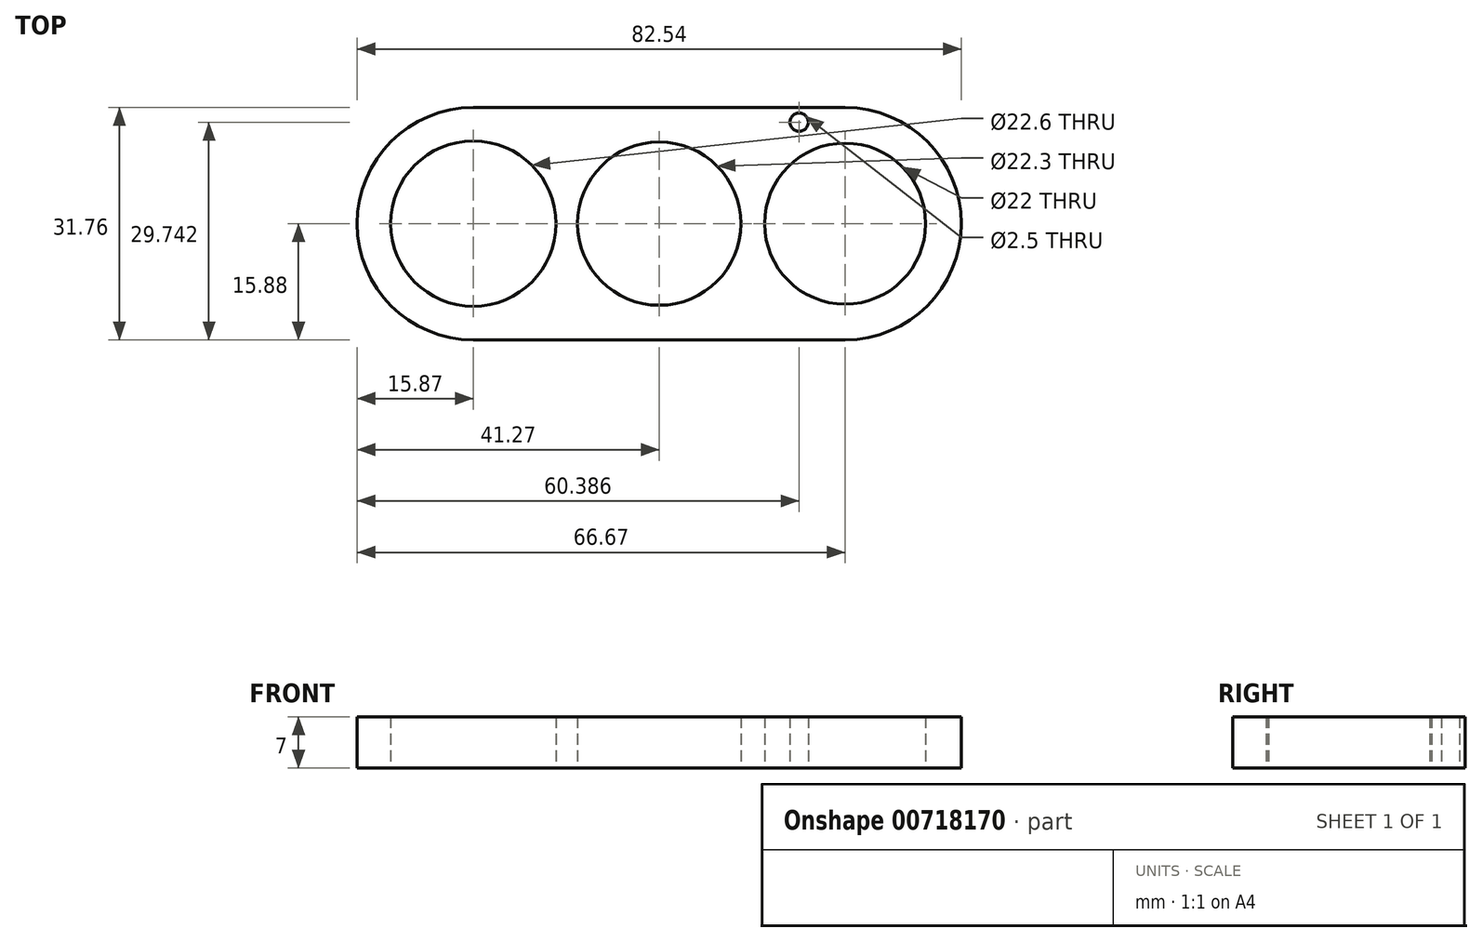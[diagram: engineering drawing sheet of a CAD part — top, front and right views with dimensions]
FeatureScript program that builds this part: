
annotation { "Feature Type Name" : "Feature", "Feature Type Description" : "" }
export const myFeature = defineFeature(function(context is Context, id is Id, definition is map)
    precondition{}
    {
        {
            var Q0;
            Q0=qCreatedBy(makeId("Top.planeOp"),FACE);
            var sketch = newSketch(context, id + "F0", { "sketchPlane" : qUnion([Q0])});
            skCircle(sketch, "E0", {"center": v(-25.4, 0) * mm, "radius": 11.3 * mm});
            skCircle(sketch, "E1", {"center": v(0, 0) * mm, "radius": 11.15 * mm});
            skCircle(sketch, "E2", {"center": v(25.4, 0) * mm, "radius": 11 * mm});
            skLineSegment(sketch, "E3", {"start": v(-25.4, 0) * mm, "end": v(0, 0) * mm, "construction": true});
            skLineSegment(sketch, "E4", {"start": v(25.4, 0) * mm, "end": v(0, 0) * mm, "construction": true});
            skLineSegment(sketch, "E5.bottom", {"start": v(-25.4, 15.88) * mm, "end": v(25.4, 15.88) * mm});
            skLineSegment(sketch, "E5.top", {"start": v(-25.4, -15.88) * mm, "end": v(25.4, -15.88) * mm});
            skLineSegment(sketch, "E5.left", {"start": v(-25.4, 15.88) * mm, "end": v(-25.4, -15.88) * mm, "construction": true});
            skLineSegment(sketch, "E5.right", {"start": v(25.4, 15.88) * mm, "end": v(25.4, -15.88) * mm, "construction": true});
            skArc(sketch, "E6", {"start": v(-25.4, 15.88) * mm, "mid": v(-41.28, 0) * mm, "end": v(-25.4, -15.88) * mm});
            skArc(sketch, "E7", {"start": v(25.4, -15.88) * mm, "mid": v(41.28, 0) * mm, "end": v(25.4, 15.88) * mm});
            skCircle(sketch, "E8", {"center": v(19.12, 13.86) * mm, "radius": 1.25 * mm});
            skSolve(sketch);
        }
        {
            var Q0;
            Q0=makeQuery(id+"F0.imprint","IMPRINT",FACE,{"disambiguationData":[TD([[makeQuery(id+"F0.imprint","IMPRINT",EDGE,{"derivedFrom":sQuery(id+"F0.wireOp",EDGE,"E0")}),-1.0]])]});
            extrude(context, id + "F1", {"entities" : qUnion([Q0]), "depth" : 7 * mm, "offsetDistance" : 25.4 * mm});
        }
    });
